FCSTD DOCUMENT  (FreeCAD 0.19R24366 (Git))
Label: hulltest4
License: All rights reserved
LicenseURL: http://en.wikipedia.org/wiki/All_rights_reserved
objects: Sketcher::SketchObject×2, PartDesign::Body×1
note: 3 computed .brp shape members not serialized (recipe doc carries the construction recipe); baked Part::Feature solids carry a one-line shape summary decoded from their .brp

FEATURE [Sketcher::SketchObject] Sketch  label="HullOutline"
  FullyConstrained = false
  Placement = pos=(0,0,0) rot=(0.980944,0.137386,0.137386;1.59004rad)
  sketch-geometry (9):
    g0: LineSegment StartX=0 StartY=4e-16 StartZ=0 EndX=160 EndY=3 EndZ=0
    g1: LineSegment StartX=0 StartY=4e-16 StartZ=0 EndX=-20 EndY=70 EndZ=0
    g2: LineSegment StartX=-20 StartY=70 StartZ=0 EndX=-170 EndY=70 EndZ=0
    g3: LineSegment StartX=-170 StartY=70 StartZ=0 EndX=-190 EndY=194.294 EndZ=0
    g4: LineSegment StartX=-190 StartY=194.294 StartZ=0 EndX=420 EndY=194.294 EndZ=0
    g5: LineSegment StartX=420 StartY=194.294 StartZ=0 EndX=180 EndY=70 EndZ=0
    g6: LineSegment StartX=180 StartY=70 StartZ=0 EndX=160 EndY=3 EndZ=0
    g7: LineSegment StartX=-20 StartY=70 StartZ=0 EndX=180 EndY=70 EndZ=0
    g8: GeomPoint X=0 Y=194.294 Z=0
  constraints (23):
    c: Coincident(g1,g0)
    c: Horizontal(g2)
    c: Coincident(g3,g2)
    c: Horizontal(g4)
    c: Coincident(g6,g5)
    c: Coincident(g6,g0)
    c: DistanceX(g4,g4) = 610
    c: Coincident(g3,g4)
    c: DistanceX(g3,g2) = 20
    c: DistanceX(g2,g1) = 150
    c: Coincident(g2,g1)
    c: DistanceY(g0,g1) = 70
    c: DistanceX(g0,g0) = 160
    c: DistanceX(g1,g0) = 20
    c: DistanceY(g0,g0) = 3
    c: Horizontal(g1,g5)
    c: DistanceX(g0,g5) = 20
    c: Coincident(g5,g4)
    c: Coincident(g-1,g0)
    c: Coincident(g7,g1)
    c: Coincident(g7,g5)
    c: PointOnObject(g8,g4)
    c: PointOnObject(g8,g-2)
FEATURE [Sketcher::SketchObject] Sketch001
  ExternalGeometry = -> [Sketch]
  FullyConstrained = false
  MapMode = 5
  Placement = pos=(0,0,0) rot=(0.57735,0.57735,0.57735;2.0944rad)
  Support = -> [YZ_Plane]
  sketch-geometry (13):
    g0: LineSegment StartX=-17.0612 StartY=0 StartZ=0 EndX=0 EndY=0 EndZ=0
    g1: LineSegment StartX=-73.1907 StartY=83.554 StartZ=0 EndX=-100.884 EndY=111.108 EndZ=0
    g2: LineSegment StartX=-100.884 StartY=111.108 StartZ=0 EndX=-118.381 EndY=144.713 EndZ=0
    g3: LineSegment StartX=-100.884 StartY=111.108 StartZ=0 EndX=0 EndY=111.108 EndZ=0
    g4: LineSegment StartX=-118.381 StartY=144.713 StartZ=0 EndX=0 EndY=144.713 EndZ=0
    g5: LineSegment StartX=-118.381 StartY=144.713 StartZ=0 EndX=-118.603 EndY=165.426 EndZ=0
    g6: LineSegment StartX=-118.603 StartY=165.426 StartZ=0 EndX=0 EndY=165.426 EndZ=0
    g7: Circle CenterX=-56.1874 CenterY=155.738 CenterZ=0 NormalX=0 NormalY=0 NormalZ=1 AngleXU=0 Radius=63.1632
    g8: LineSegment StartX=-52.197 StartY=194.294 StartZ=0 EndX=-106.217 EndY=194.294 EndZ=0
    g9: LineSegment StartX=-43.8724 StartY=36.2065 StartZ=0 EndX=0 EndY=36.2065 EndZ=0
    g10: LineSegment StartX=-26.871 StartY=14.0643 StartZ=0 EndX=0 EndY=14.0643 EndZ=0
    g11: LineSegment StartX=0 StartY=60.3634 StartZ=0 EndX=-57.4003 EndY=60.3634 EndZ=0
    g12: LineSegment StartX=-73.1907 StartY=83.554 StartZ=0 EndX=0 EndY=83.554 EndZ=0
  constraints (27):
    c: Coincident(g0,g-1)
    c: Coincident(g2,g1)
    c: Coincident(g3,g1)
    c: PointOnObject(g3,g-2)
    c: Horizontal(g3)
    c: Coincident(g4,g2)
    c: PointOnObject(g4,g-2)
    c: Horizontal(g4)
    c: Coincident(g5,g2)
    c: PointOnObject(g6,g-2)
    c: Horizontal(g6)
    c: PointOnObject(g6,g7)
    c: Coincident(g5,g6)
    c: PointOnObject(g2,g7)
    c: PointOnObject(g1,g7)
    c: Coincident(g8,g-3)
    c: PointOnObject(g8,g7)
    c: Horizontal(g8)
    c: Horizontal(g9)
    c: Horizontal(g10)
    c: Horizontal(g11)
    c: Coincident(g12,g1)
    c: Horizontal(g12)
    c: Vertical(g12,g11)
    c: Vertical(g11,g9)
    c: Vertical(g9,g10)
    c: Vertical(g10,g0)
FEATURE [PartDesign::Body] Body
  Group = -> [Sketch,Sketch001]
  Origin = -> Origin
